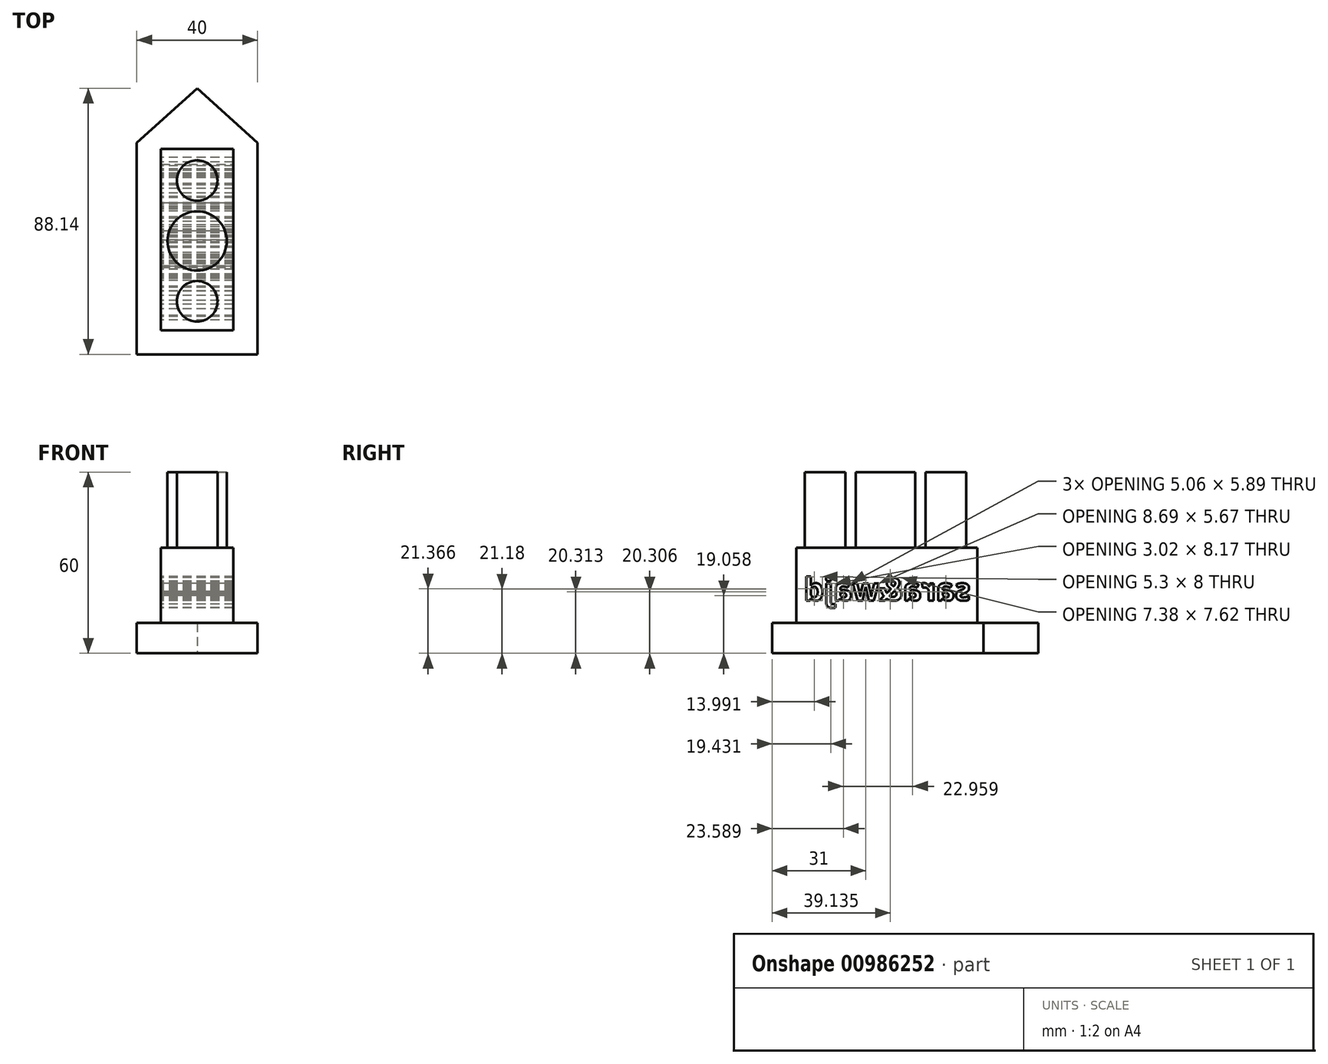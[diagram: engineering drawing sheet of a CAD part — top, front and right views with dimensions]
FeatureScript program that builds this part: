
annotation { "Feature Type Name" : "Feature", "Feature Type Description" : "" }
export const myFeature = defineFeature(function(context is Context, id is Id, definition is map)
    precondition{}
    {
        {
            var Q0;
            Q0=qCreatedBy(makeId("Top.planeOp"),FACE);
            var sketch = newSketch(context, id + "F0", { "sketchPlane" : qUnion([Q0])});
            skLineSegment(sketch, "E0", {"start": v(-20, 32.44) * mm, "end": v(-20, -37.56) * mm});
            skLineSegment(sketch, "E1", {"start": v(-20, -37.56) * mm, "end": v(20, -37.56) * mm});
            skLineSegment(sketch, "E2", {"start": v(20, -37.56) * mm, "end": v(20, 32.44) * mm});
            skLineSegment(sketch, "E3", {"start": v(-20, 32.44) * mm, "end": v(0, 50.58) * mm});
            skLineSegment(sketch, "E4", {"start": v(0, 50.58) * mm, "end": v(20, 32.44) * mm});
            skSolve(sketch);
        }
        {
            var Q0;
            Q0=makeQuery(id+"F0.imprint","IMPRINT",FACE,{"disambiguationData":[TD([[makeQuery(id+"F0.imprint","IMPRINT",EDGE,{"derivedFrom":sQuery(id+"F0.wireOp",EDGE,"E0")}),1.0]])]});
            extrude(context, id + "F1", {"entities" : qUnion([Q0]), "depth" : 10 * mm, "offsetDistance" : 25 * mm});
        }
        {
            var Q0;
            Q0=makeQuery(id+"F1.opExtrude","CAP_FACE",FACE,{"disambiguationData":[OSD([sQuery(id+"F0.wireOp",EDGE,"E0"),sQuery(id+"F0.wireOp",EDGE,"E1"),sQuery(id+"F0.wireOp",EDGE,"E2"),sQuery(id+"F0.wireOp",EDGE,"E3"),sQuery(id+"F0.wireOp",EDGE,"E4")])],"isStart":false});
            var sketch = newSketch(context, id + "F2", { "sketchPlane" : qUnion([Q0])});
            skLineSegment(sketch, "E5", {"start": v(-12, -29.56) * mm, "end": v(12, -29.56) * mm});
            skLineSegment(sketch, "E6", {"start": v(12, -29.56) * mm, "end": v(12, 30.44) * mm});
            skLineSegment(sketch, "E7", {"start": v(-12, -29.56) * mm, "end": v(-12, 30.44) * mm});
            skLineSegment(sketch, "E8", {"start": v(-12, 30.44) * mm, "end": v(12, 30.44) * mm});
            skSolve(sketch);
        }
        {
            var Q0;
            Q0=makeQuery(id+"F2.imprint","IMPRINT",FACE,{"disambiguationData":[TD([[makeQuery(id+"F2.imprint","IMPRINT",EDGE,{"derivedFrom":sQuery(id+"F2.wireOp",EDGE,"E5")}),1.0]])]});
            extrude(context, id + "F3", {"entities" : qUnion([Q0]), "operationType" : NewBodyOperationType.ADD, "depth" : 25 * mm, "offsetDistance" : 25 * mm});
        }
        {
            var Q0;
            Q0=makeQuery(id+"F3.opExtrude","CAP_FACE",FACE,{"disambiguationData":[OSD([sQuery(id+"F2.wireOp",EDGE,"E5"),sQuery(id+"F2.wireOp",EDGE,"E6"),sQuery(id+"F2.wireOp",EDGE,"E7"),sQuery(id+"F2.wireOp",EDGE,"E8")])],"isStart":false});
            var sketch = newSketch(context, id + "F4", { "sketchPlane" : qUnion([Q0])});
            skCircle(sketch, "E9", {"center": v(0, 20) * mm, "radius": 6.73 * mm});
            skCircle(sketch, "E10", {"center": v(0, 0) * mm, "radius": 9.81 * mm});
            skCircle(sketch, "E11", {"center": v(0, -20) * mm, "radius": 6.73 * mm});
            skSolve(sketch);
        }
        {
            var Q0;
            Q0 = qSketchRegion(id + "F4", true);
            extrude(context, id + "F5", {"entities" : qUnion([Q0]), "operationType" : NewBodyOperationType.ADD, "depth" : 25 * mm, "offsetDistance" : 25 * mm});
        }
        {
            var Q0;
            Q0=makeQuery(id+"F3.opExtrude","SWEPT_FACE",FACE,{"disambiguationData":[OSD([sQuery(id+"F2.wireOp",EDGE,"E7")])]});
            var sketch = newSketch(context, id + "F6", { "sketchPlane" : qUnion([Q0])});
            skText(sketch, "E12", { "text": "sara&wajd", "fontName": "OpenSans-Bold.ttf"});
            const initialGuessF6  = {"E12": [-0.02811, 0.01747, 1, 0, 0.00748]};
            skSetInitialGuess(sketch, initialGuessF6);
            skSolve(sketch);
        }
        {
            var Q0;
            Q0 = qSketchRegion(id + "F6", true);
            extrude(context, id + "F7", {"entities" : qUnion([Q0]), "operationType" : NewBodyOperationType.REMOVE, "oppositeDirection" : true, "depth" : 25 * mm, "offsetDistance" : 25 * mm});
        }
    });
